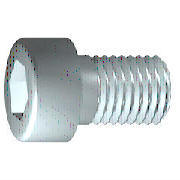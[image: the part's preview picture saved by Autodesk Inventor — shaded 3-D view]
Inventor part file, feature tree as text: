
AUTODESK INVENTOR PART (.ipt)
format: ipt  version: 2023.3 (Build 273359000, 359)  size: 196,096 bytes
history: native  units: mm (DEFAULTED — no unit token found)
features: sketch x2, other x1, extrude x1, plane x1, fillet x1
ambient origin geometry x7: Origin, YZ Plane, XY Plane, X Axis, Y Axis, Z Axis, Center Point
bodies: Solid1 (feature_tree)
feature tree (6):
  other  "Körper"
  extrude  "Loch"  Depth=3.0mm
  plane  "Work Plane1"
  fillet  "Fillet2"  Radius=3.0mm
  sketch  "Skizze1"  dims[d1=3.75mm d2=0.306825mm d3=3.0mm]
  sketch  "Skizze2"  dims[d4=1.3mm d5=60.0deg d6=3.0mm d7=3.0mm d8=2.886751mm d9=5.5mm d10=90.0deg d11=10.0mm d12=0.0mm d13=3.75mm d14=0.0mm d15=0.306725mm d16=0.306725mm d17=0.3mm d19=0.0mm d26=5.0mm d27=45.0deg d28=0.0mm d29=0.0mm d30=0.1mm]
